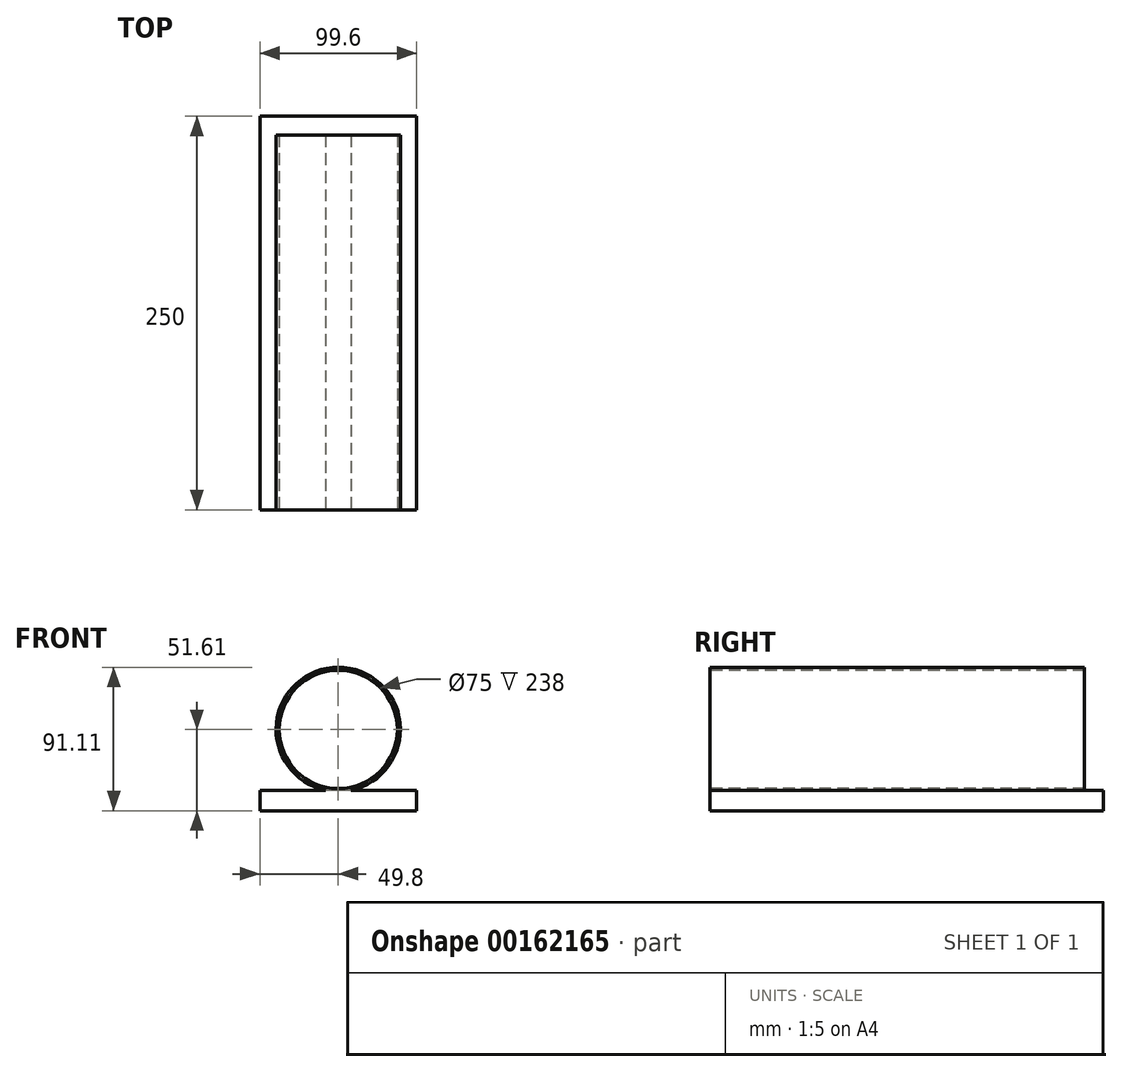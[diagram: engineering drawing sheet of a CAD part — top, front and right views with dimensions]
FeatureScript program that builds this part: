
annotation { "Feature Type Name" : "Feature", "Feature Type Description" : "" }
export const myFeature = defineFeature(function(context is Context, id is Id, definition is map)
    precondition{}
    {
        {
            var Q0;
            Q0=qCreatedBy(makeId("Front.planeOp"),FACE);
            var sketch = newSketch(context, id + "F0", { "sketchPlane" : qUnion([Q0])});
            skCircle(sketch, "E0", {"center": v(0, 0) * mm, "radius": 37.5 * mm});
            skCircle(sketch, "E1.0", {"center": v(0, 0) * mm, "radius": 39.5 * mm});
            skSolve(sketch);
        }
        {
            var Q0;
            Q0=makeQuery(id+"F0.imprint","IMPRINT",FACE,{"disambiguationData":[TD([[makeQuery(id+"F0.imprint","IMPRINT",EDGE,{"derivedFrom":sQuery(id+"F0.wireOp",EDGE,"E0")}),-1.0]])]});
            extrude(context, id + "F1", {"entities" : qUnion([Q0]), "oppositeDirection" : true, "depth" : 238 * mm});
        }
        {
            var Q0;
            Q0=qCreatedBy(makeId("Front.planeOp"),FACE);
            var sketch = newSketch(context, id + "F2", { "sketchPlane" : qUnion([Q0])});
            skLineSegment(sketch, "E2.bottom", {"start": v(49.8, -51.61) * mm, "end": v(-49.8, -51.61) * mm});
            skLineSegment(sketch, "E2.top", {"start": v(49.8, -38.67) * mm, "end": v(-49.8, -38.67) * mm});
            skLineSegment(sketch, "E2.left", {"start": v(49.8, -51.61) * mm, "end": v(49.8, -38.67) * mm});
            skLineSegment(sketch, "E2.right", {"start": v(-49.8, -51.61) * mm, "end": v(-49.8, -38.67) * mm});
            skPoint(sketch, "E2.middle", {"position": v(0, -45.14) * mm});
            skSolve(sketch);
        }
        {
            var Q0;
            Q0=makeQuery(id+"F2.imprint","IMPRINT",FACE,{"disambiguationData":[TD([[makeQuery(id+"F2.imprint","IMPRINT",EDGE,{"derivedFrom":sQuery(id+"F2.wireOp",EDGE,"E2.bottom")}),-1.0]])]});
            extrude(context, id + "F3", {"entities" : qUnion([Q0]), "operationType" : NewBodyOperationType.ADD, "oppositeDirection" : true, "depth" : 250 * mm});
        }
    });
